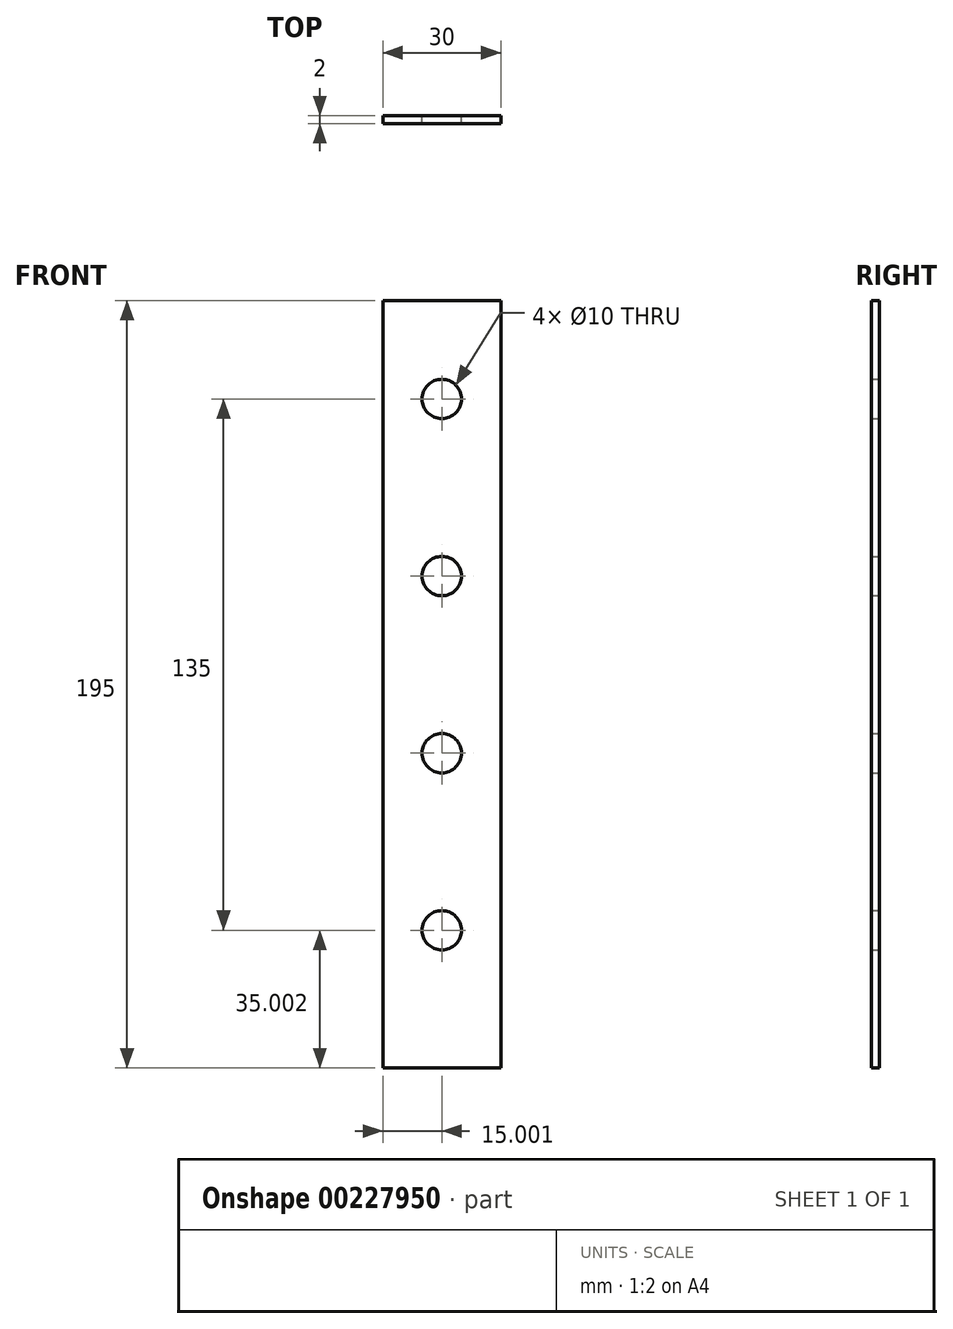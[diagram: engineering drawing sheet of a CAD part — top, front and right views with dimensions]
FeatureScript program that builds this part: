
annotation { "Feature Type Name" : "Feature", "Feature Type Description" : "" }
export const myFeature = defineFeature(function(context is Context, id is Id, definition is map)
    precondition{}
    {
        {
            var Q0;
            Q0=qCreatedBy(makeId("Front.planeOp"),FACE);
            var sketch = newSketch(context, id + "F0", { "sketchPlane" : qUnion([Q0])});
            skLineSegment(sketch, "E0.bottom", {"start": v(-63.7, 96.76) * mm, "end": v(-33.7, 96.76) * mm});
            skLineSegment(sketch, "E0.top", {"start": v(-63.7, -98.24) * mm, "end": v(-33.7, -98.24) * mm});
            skLineSegment(sketch, "E0.left", {"start": v(-63.7, 96.76) * mm, "end": v(-63.7, -98.24) * mm});
            skLineSegment(sketch, "E0.right", {"start": v(-33.7, 96.76) * mm, "end": v(-33.7, -98.24) * mm});
            skCircle(sketch, "E1", {"center": v(-48.7, 71.76) * mm, "radius": 5 * mm});
            skCircle(sketch, "E2", {"center": v(-48.7, 26.76) * mm, "radius": 5 * mm});
            skCircle(sketch, "E3", {"center": v(-48.7, -18.24) * mm, "radius": 5 * mm});
            skCircle(sketch, "E4", {"center": v(-48.7, -63.24) * mm, "radius": 5 * mm});
            skSolve(sketch);
        }
        {
            var Q0;
            Q0 = qSketchRegion(id + "F0", true);
            extrude(context, id + "F1", {"entities" : qUnion([Q0]), "depth" : 2 * mm});
        }
    });
